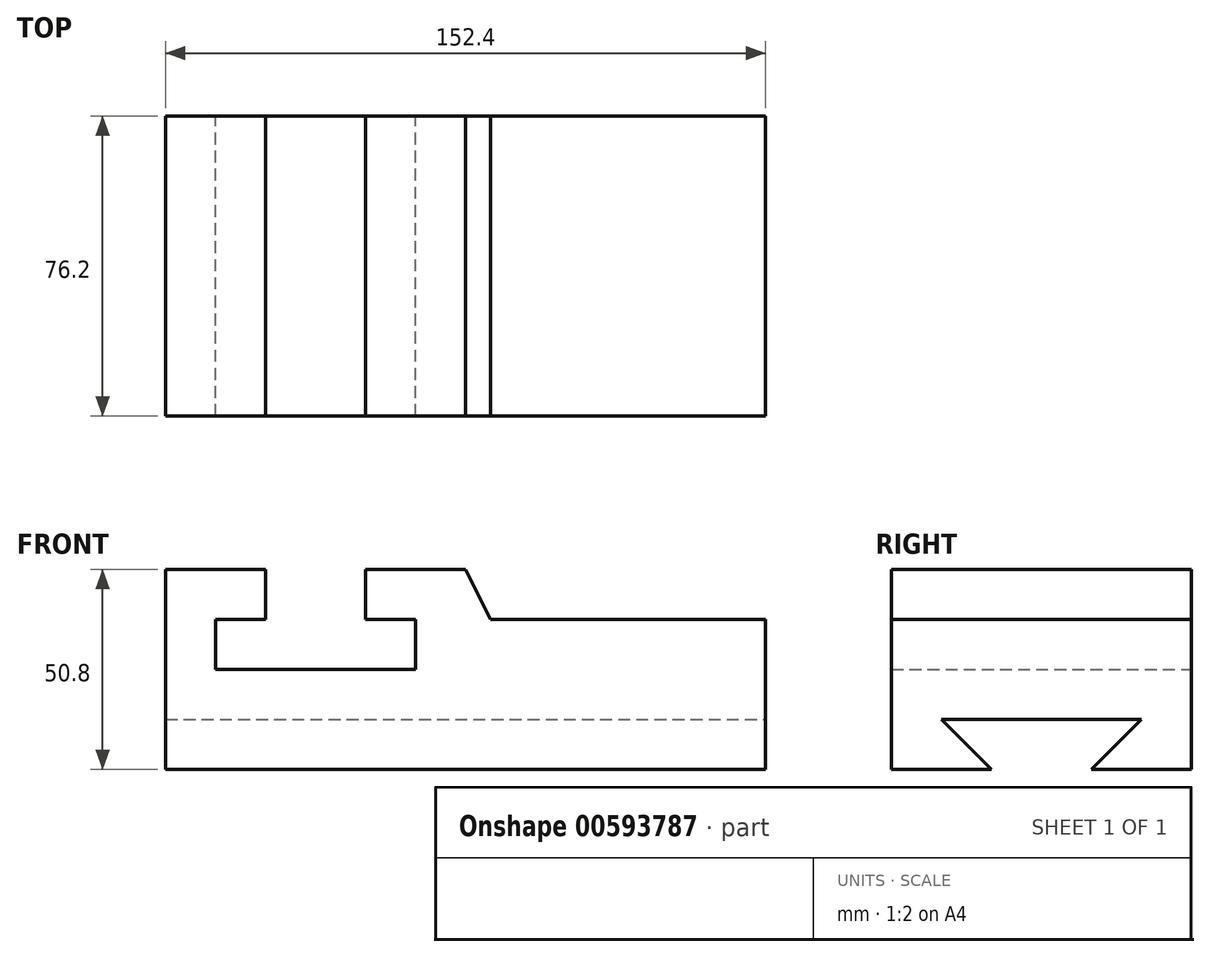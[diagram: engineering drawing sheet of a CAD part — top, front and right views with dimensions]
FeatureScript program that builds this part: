
annotation { "Feature Type Name" : "Feature", "Feature Type Description" : "" }
export const myFeature = defineFeature(function(context is Context, id is Id, definition is map)
    precondition{}
    {
        {
            var Q0;
            Q0=qCreatedBy(makeId("Front.planeOp"),FACE);
            var sketch = newSketch(context, id + "F0", { "sketchPlane" : qUnion([Q0])});
            skLineSegment(sketch, "E0", {"start": v(0, 0) * mm, "end": v(152.4, 0) * mm});
            skLineSegment(sketch, "E1", {"start": v(152.4, 0) * mm, "end": v(152.4, 38.1) * mm});
            skLineSegment(sketch, "E2", {"start": v(152.4, 38.1) * mm, "end": v(82.55, 38.1) * mm});
            skLineSegment(sketch, "E3", {"start": v(0, 0) * mm, "end": v(0, 50.8) * mm});
            skLineSegment(sketch, "E4", {"start": v(0, 50.8) * mm, "end": v(25.4, 50.8) * mm});
            skLineSegment(sketch, "E5", {"start": v(25.4, 50.8) * mm, "end": v(25.4, 38.1) * mm});
            skLineSegment(sketch, "E6", {"start": v(25.4, 38.1) * mm, "end": v(12.7, 38.1) * mm});
            skLineSegment(sketch, "E7", {"start": v(12.7, 38.1) * mm, "end": v(12.7, 25.4) * mm});
            skLineSegment(sketch, "E8", {"start": v(12.7, 25.4) * mm, "end": v(63.5, 25.4) * mm});
            skLineSegment(sketch, "E9", {"start": v(63.5, 25.4) * mm, "end": v(63.5, 38.1) * mm});
            skLineSegment(sketch, "E10", {"start": v(63.5, 38.1) * mm, "end": v(50.8, 38.1) * mm});
            skLineSegment(sketch, "E11", {"start": v(50.8, 38.1) * mm, "end": v(50.8, 50.8) * mm});
            skLineSegment(sketch, "E12", {"start": v(50.8, 50.8) * mm, "end": v(76.2, 50.8) * mm});
            skLineSegment(sketch, "E13", {"start": v(76.2, 50.8) * mm, "end": v(82.55, 38.1) * mm});
            skSolve(sketch);
        }
        {
            var Q0;
            Q0=makeQuery(id+"F0.imprint","IMPRINT",FACE,{"disambiguationData":[TD([[makeQuery(id+"F0.imprint","IMPRINT",EDGE,{"derivedFrom":sQuery(id+"F0.wireOp",EDGE,"E0")}),1.0]])]});
            extrude(context, id + "F1", {"entities" : qUnion([Q0]), "depth" : 76.2 * mm, "offsetDistance" : 25.4 * mm});
        }
        {
            var Q0;
            Q0=makeQuery(id+"F1.opExtrude","SWEPT_FACE",FACE,{"disambiguationData":[OSD([sQuery(id+"F0.wireOp",EDGE,"E1")])]});
            var sketch = newSketch(context, id + "F2", { "sketchPlane" : qUnion([Q0])});
            skLineSegment(sketch, "E14", {"start": v(0, 0) * mm, "end": v(-25.4, 0) * mm});
            skLineSegment(sketch, "E15", {"start": v(-25.4, 0) * mm, "end": v(-12.7, 12.7) * mm});
            skLineSegment(sketch, "E16", {"start": v(-12.7, 12.7) * mm, "end": v(-63.5, 12.7) * mm});
            skLineSegment(sketch, "E17", {"start": v(-76.2, 0) * mm, "end": v(-50.8, 0) * mm});
            skLineSegment(sketch, "E18", {"start": v(-50.8, 0) * mm, "end": v(-63.5, 12.7) * mm});
            skSolve(sketch);
        }
        {
            var Q0;
            Q0 = qSketchRegion(id + "F2", true);
            var Q1;
            {var subQ0=sQuery(id+"F2.wireOp",EDGE,"E15");Q1=makeQuery(id+"F2.imprint","IMPRINT",FACE,{"disambiguationData":[TD([[makeQuery(id+"F2.imprint","IMPRINT",EDGE,{"derivedFrom":subQ0}),1.0]])]});}
            extrude(context, id + "F3", {"entities" : qUnion([Q0, Q1]), "operationType" : NewBodyOperationType.REMOVE, "oppositeDirection" : true, "depth" : 182.37 * mm, "offsetDistance" : 25.4 * mm});
        }
    });
